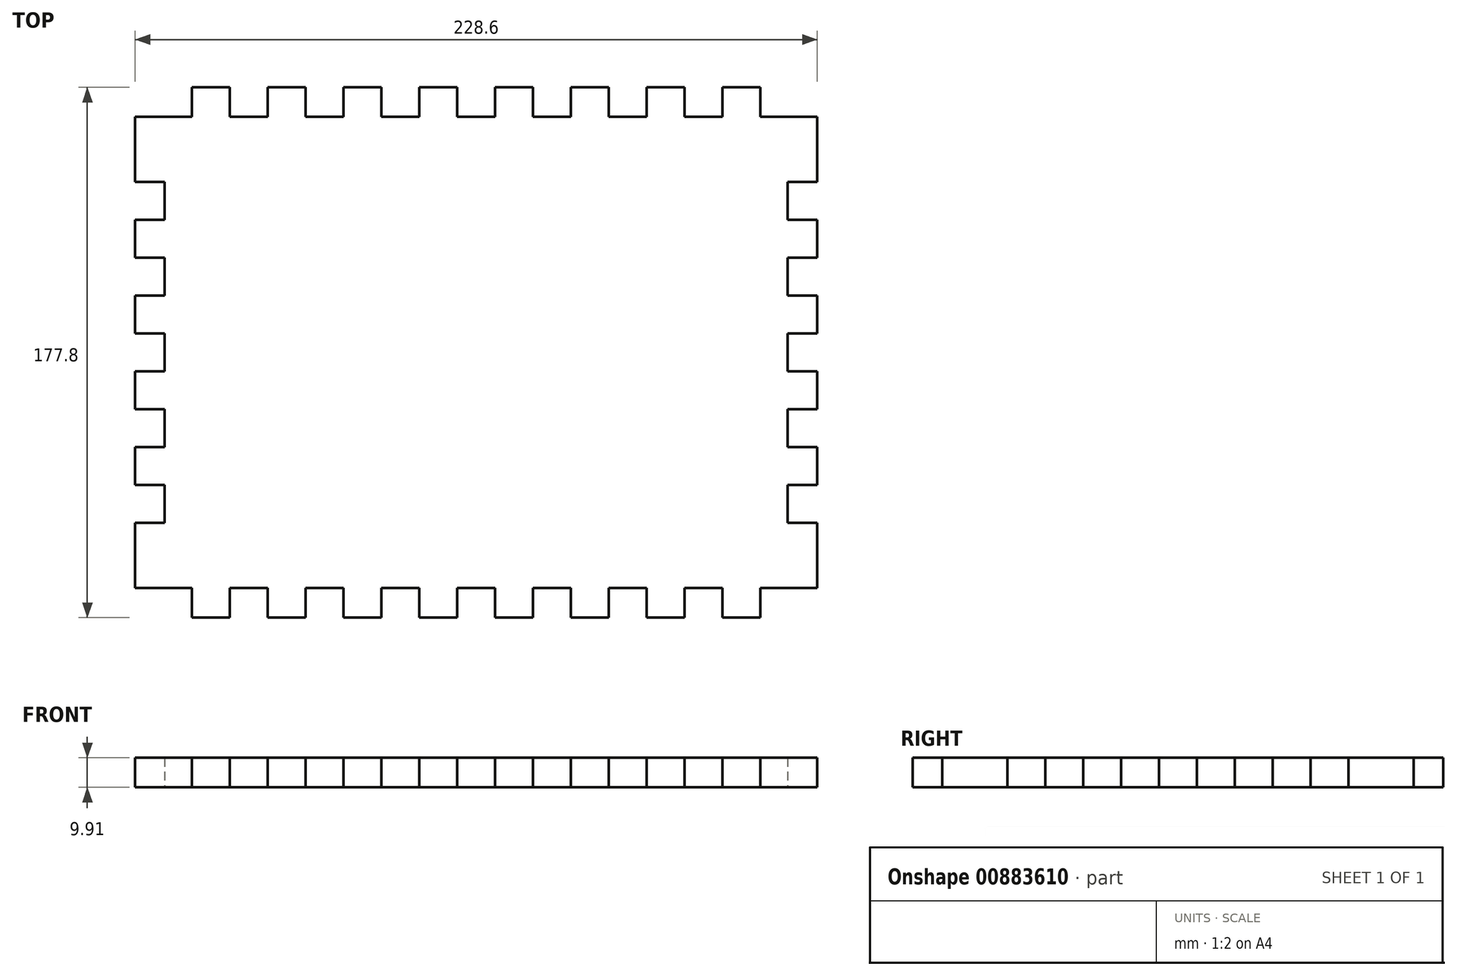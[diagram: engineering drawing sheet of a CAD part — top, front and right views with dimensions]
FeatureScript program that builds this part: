
annotation { "Feature Type Name" : "Feature", "Feature Type Description" : "" }
export const myFeature = defineFeature(function(context is Context, id is Id, definition is map)
    precondition{}
    {
        {
            var Q0;
            Q0=qCreatedBy(makeId("Top.planeOp"),FACE);
            var sketch = newSketch(context, id + "F0", { "sketchPlane" : qUnion([Q0])});
            skLineSegment(sketch, "E0", {"start": v(19.05, -9.9) * mm, "end": v(19.05, 0) * mm});
            skLineSegment(sketch, "E1", {"start": v(19.05, 0) * mm, "end": v(31.75, 0) * mm});
            skLineSegment(sketch, "E2", {"start": v(31.75, 0) * mm, "end": v(31.75, -9.9) * mm});
            skLineSegment(sketch, "E3", {"start": v(31.75, -9.9) * mm, "end": v(44.45, -9.9) * mm});
            skLineSegment(sketch, "E4", {"start": v(44.45, -9.9) * mm, "end": v(44.45, 0) * mm});
            skLineSegment(sketch, "E5", {"start": v(44.45, 0) * mm, "end": v(57.15, 0) * mm});
            skLineSegment(sketch, "E6", {"start": v(57.15, 0) * mm, "end": v(57.15, -9.9) * mm});
            skLineSegment(sketch, "E7", {"start": v(57.15, -9.9) * mm, "end": v(69.85, -9.9) * mm});
            skLineSegment(sketch, "E8", {"start": v(69.85, -9.9) * mm, "end": v(69.85, 0) * mm});
            skLineSegment(sketch, "E9", {"start": v(69.85, 0) * mm, "end": v(82.55, 0) * mm});
            skLineSegment(sketch, "E10", {"start": v(82.55, 0) * mm, "end": v(82.55, -9.9) * mm});
            skLineSegment(sketch, "E11", {"start": v(82.55, -9.9) * mm, "end": v(95.25, -9.9) * mm});
            skLineSegment(sketch, "E12", {"start": v(95.25, -9.9) * mm, "end": v(95.25, 0) * mm});
            skLineSegment(sketch, "E13", {"start": v(95.25, 0) * mm, "end": v(107.95, 0) * mm});
            skLineSegment(sketch, "E14", {"start": v(107.95, 0) * mm, "end": v(107.95, -9.9) * mm});
            skLineSegment(sketch, "E15", {"start": v(107.95, -9.9) * mm, "end": v(120.65, -9.9) * mm});
            skLineSegment(sketch, "E16", {"start": v(120.65, -9.9) * mm, "end": v(120.65, 0) * mm});
            skLineSegment(sketch, "E17", {"start": v(120.65, 0) * mm, "end": v(133.35, 0) * mm});
            skLineSegment(sketch, "E18", {"start": v(133.35, 0) * mm, "end": v(133.35, -9.9) * mm});
            skLineSegment(sketch, "E19", {"start": v(133.35, -9.9) * mm, "end": v(146.05, -9.9) * mm});
            skLineSegment(sketch, "E20", {"start": v(146.05, -9.9) * mm, "end": v(146.05, 0) * mm});
            skLineSegment(sketch, "E21", {"start": v(146.05, 0) * mm, "end": v(158.75, 0) * mm});
            skLineSegment(sketch, "E22", {"start": v(158.75, 0) * mm, "end": v(158.75, -9.9) * mm});
            skLineSegment(sketch, "E23", {"start": v(158.75, -9.9) * mm, "end": v(171.45, -9.9) * mm});
            skLineSegment(sketch, "E24", {"start": v(171.45, -9.9) * mm, "end": v(171.45, 0) * mm});
            skLineSegment(sketch, "E25", {"start": v(171.45, 0) * mm, "end": v(184.15, 0) * mm});
            skLineSegment(sketch, "E26", {"start": v(184.15, 0) * mm, "end": v(184.15, -9.9) * mm});
            skLineSegment(sketch, "E27", {"start": v(184.15, -9.9) * mm, "end": v(196.85, -9.9) * mm});
            skLineSegment(sketch, "E28", {"start": v(196.85, -9.9) * mm, "end": v(196.85, 0) * mm});
            skLineSegment(sketch, "E29", {"start": v(196.85, 0) * mm, "end": v(209.55, 0) * mm});
            skLineSegment(sketch, "E30", {"start": v(209.55, 0) * mm, "end": v(209.55, -9.9) * mm});
            skPoint(sketch, "E31.orphan", {"position": v(0, 0) * mm});
            skPoint(sketch, "E32.orphan", {"position": v(0, -9.9) * mm});
            skLineSegment(sketch, "E33", {"start": v(0, -31.75) * mm, "end": v(9.9, -31.75) * mm});
            skLineSegment(sketch, "E34", {"start": v(9.9, -31.75) * mm, "end": v(9.9, -44.45) * mm});
            skLineSegment(sketch, "E35", {"start": v(9.9, -44.45) * mm, "end": v(0, -44.45) * mm});
            skLineSegment(sketch, "E36", {"start": v(0, -44.45) * mm, "end": v(0, -57.15) * mm});
            skLineSegment(sketch, "E37", {"start": v(0, -57.15) * mm, "end": v(9.9, -57.15) * mm});
            skLineSegment(sketch, "E38", {"start": v(9.9, -57.15) * mm, "end": v(9.9, -69.85) * mm});
            skLineSegment(sketch, "E39", {"start": v(9.9, -69.85) * mm, "end": v(0, -69.85) * mm});
            skLineSegment(sketch, "E40", {"start": v(0, -69.85) * mm, "end": v(0, -82.55) * mm});
            skLineSegment(sketch, "E41", {"start": v(0, -82.55) * mm, "end": v(9.9, -82.55) * mm});
            skLineSegment(sketch, "E42", {"start": v(9.9, -82.55) * mm, "end": v(9.9, -95.25) * mm});
            skLineSegment(sketch, "E43", {"start": v(9.9, -95.25) * mm, "end": v(0, -95.25) * mm});
            skLineSegment(sketch, "E44.trimOffspring", {"start": v(0, -95.25) * mm, "end": v(0, -107.95) * mm});
            skLineSegment(sketch, "E45", {"start": v(0, -107.95) * mm, "end": v(9.9, -107.95) * mm});
            skLineSegment(sketch, "E46", {"start": v(9.9, -107.95) * mm, "end": v(9.9, -120.65) * mm});
            skLineSegment(sketch, "E47", {"start": v(9.9, -120.65) * mm, "end": v(0, -120.65) * mm});
            skLineSegment(sketch, "E48", {"start": v(0, -120.65) * mm, "end": v(0, -133.35) * mm});
            skLineSegment(sketch, "E49", {"start": v(0, -133.35) * mm, "end": v(9.9, -133.35) * mm});
            skLineSegment(sketch, "E50", {"start": v(9.9, -133.35) * mm, "end": v(9.9, -146.05) * mm});
            skLineSegment(sketch, "E51", {"start": v(9.9, -146.05) * mm, "end": v(0, -146.05) * mm});
            skLineSegment(sketch, "E52", {"start": v(114.3, -9.9) * mm, "end": v(114.3, -13.72) * mm, "construction": true});
            skLineSegment(sketch, "E53.MirrorCS", {"start": v(228.6, -95.25) * mm, "end": v(228.6, -107.95) * mm});
            skLineSegment(sketch, "E54.MirrorCS", {"start": v(228.6, -44.45) * mm, "end": v(228.6, -57.15) * mm});
            skLineSegment(sketch, "E55.MirrorCS", {"start": v(228.6, -120.65) * mm, "end": v(228.6, -133.35) * mm});
            skLineSegment(sketch, "E56.MirrorCS", {"start": v(228.6, -69.85) * mm, "end": v(228.6, -82.55) * mm});
            skLineSegment(sketch, "E57.MirrorCS", {"start": v(228.6, -107.95) * mm, "end": v(218.7, -107.95) * mm});
            skLineSegment(sketch, "E58.MirrorCS", {"start": v(228.6, -82.55) * mm, "end": v(218.7, -82.55) * mm});
            skLineSegment(sketch, "E59.MirrorCS", {"start": v(228.6, -133.35) * mm, "end": v(218.7, -133.35) * mm});
            skLineSegment(sketch, "E60.MirrorCS", {"start": v(218.7, -69.85) * mm, "end": v(228.6, -69.85) * mm});
            skLineSegment(sketch, "E61.MirrorCS", {"start": v(218.7, -107.95) * mm, "end": v(218.7, -120.65) * mm});
            skLineSegment(sketch, "E62.MirrorCS", {"start": v(228.6, -57.15) * mm, "end": v(218.7, -57.15) * mm});
            skLineSegment(sketch, "E63.MirrorCS", {"start": v(218.7, -120.65) * mm, "end": v(228.6, -120.65) * mm});
            skLineSegment(sketch, "E64.MirrorCS", {"start": v(218.7, -95.25) * mm, "end": v(228.6, -95.25) * mm});
            skLineSegment(sketch, "E65.MirrorCS", {"start": v(218.7, -57.15) * mm, "end": v(218.7, -69.85) * mm});
            skLineSegment(sketch, "E66.MirrorCS", {"start": v(218.7, -44.45) * mm, "end": v(228.6, -44.45) * mm});
            skLineSegment(sketch, "E67.MirrorCS", {"start": v(218.7, -133.35) * mm, "end": v(218.7, -146.05) * mm});
            skLineSegment(sketch, "E68.MirrorCS", {"start": v(218.7, -146.05) * mm, "end": v(228.6, -146.05) * mm});
            skLineSegment(sketch, "E69.MirrorCS", {"start": v(228.6, -31.75) * mm, "end": v(218.7, -31.75) * mm});
            skLineSegment(sketch, "E70.MirrorCS", {"start": v(218.7, -82.55) * mm, "end": v(218.7, -95.25) * mm});
            skLineSegment(sketch, "E71.MirrorCS", {"start": v(218.7, -31.75) * mm, "end": v(218.7, -44.45) * mm});
            skLineSegment(sketch, "E72", {"start": v(9.9, -88.9) * mm, "end": v(13.72, -88.9) * mm, "construction": true});
            skLineSegment(sketch, "E73.MirrorCS", {"start": v(209.55, -177.8) * mm, "end": v(209.55, -167.9) * mm});
            skLineSegment(sketch, "E74.MirrorCS", {"start": v(158.75, -177.8) * mm, "end": v(158.75, -167.9) * mm});
            skLineSegment(sketch, "E75.MirrorCS", {"start": v(146.05, -167.9) * mm, "end": v(146.05, -177.8) * mm});
            skLineSegment(sketch, "E76.MirrorCS", {"start": v(19.05, -167.9) * mm, "end": v(19.05, -177.8) * mm});
            skLineSegment(sketch, "E77.MirrorCS", {"start": v(69.85, -167.9) * mm, "end": v(69.85, -177.8) * mm});
            skLineSegment(sketch, "E78.MirrorCS", {"start": v(196.85, -167.9) * mm, "end": v(196.85, -177.8) * mm});
            skLineSegment(sketch, "E79.MirrorCS", {"start": v(82.55, -177.8) * mm, "end": v(82.55, -167.9) * mm});
            skLineSegment(sketch, "E80.MirrorCS", {"start": v(171.45, -167.9) * mm, "end": v(171.45, -177.8) * mm});
            skLineSegment(sketch, "E81.MirrorCS", {"start": v(146.05, -177.8) * mm, "end": v(158.75, -177.8) * mm});
            skLineSegment(sketch, "E82.MirrorCS", {"start": v(107.95, -177.8) * mm, "end": v(107.95, -167.9) * mm});
            skLineSegment(sketch, "E83.MirrorCS", {"start": v(120.65, -167.9) * mm, "end": v(120.65, -177.8) * mm});
            skLineSegment(sketch, "E84.MirrorCS", {"start": v(95.25, -167.9) * mm, "end": v(95.25, -177.8) * mm});
            skLineSegment(sketch, "E85.MirrorCS", {"start": v(44.45, -167.9) * mm, "end": v(44.45, -177.8) * mm});
            skLineSegment(sketch, "E86.MirrorCS", {"start": v(31.75, -177.8) * mm, "end": v(31.75, -167.9) * mm});
            skLineSegment(sketch, "E87.MirrorCS", {"start": v(184.15, -177.8) * mm, "end": v(184.15, -167.9) * mm});
            skLineSegment(sketch, "E88.MirrorCS", {"start": v(133.35, -177.8) * mm, "end": v(133.35, -167.9) * mm});
            skLineSegment(sketch, "E89.MirrorCS", {"start": v(57.15, -177.8) * mm, "end": v(57.15, -167.9) * mm});
            skLineSegment(sketch, "E90.MirrorCS", {"start": v(107.95, -167.9) * mm, "end": v(120.65, -167.9) * mm});
            skLineSegment(sketch, "E91.MirrorCS", {"start": v(19.05, -177.8) * mm, "end": v(31.75, -177.8) * mm});
            skLineSegment(sketch, "E92.MirrorCS", {"start": v(31.75, -167.9) * mm, "end": v(44.45, -167.9) * mm});
            skLineSegment(sketch, "E93.MirrorCS", {"start": v(95.25, -177.8) * mm, "end": v(107.95, -177.8) * mm});
            skLineSegment(sketch, "E94.MirrorCS", {"start": v(196.85, -177.8) * mm, "end": v(209.55, -177.8) * mm});
            skLineSegment(sketch, "E95.MirrorCS", {"start": v(158.75, -167.9) * mm, "end": v(171.45, -167.9) * mm});
            skLineSegment(sketch, "E96.MirrorCS", {"start": v(133.35, -167.9) * mm, "end": v(146.05, -167.9) * mm});
            skLineSegment(sketch, "E97.MirrorCS", {"start": v(171.45, -177.8) * mm, "end": v(184.15, -177.8) * mm});
            skLineSegment(sketch, "E98.MirrorCS", {"start": v(69.85, -177.8) * mm, "end": v(82.55, -177.8) * mm});
            skLineSegment(sketch, "E99.MirrorCS", {"start": v(44.45, -177.8) * mm, "end": v(57.15, -177.8) * mm});
            skLineSegment(sketch, "E100.MirrorCS", {"start": v(184.15, -167.9) * mm, "end": v(196.85, -167.9) * mm});
            skLineSegment(sketch, "E101.MirrorCS", {"start": v(82.55, -167.9) * mm, "end": v(95.25, -167.9) * mm});
            skLineSegment(sketch, "E102.MirrorCS", {"start": v(120.65, -177.8) * mm, "end": v(133.35, -177.8) * mm});
            skLineSegment(sketch, "E103.MirrorCS", {"start": v(57.15, -167.9) * mm, "end": v(69.85, -167.9) * mm});
            skLineSegment(sketch, "E104", {"start": v(0, -9.9) * mm, "end": v(0, -31.75) * mm});
            skLineSegment(sketch, "E105", {"start": v(0, -9.9) * mm, "end": v(19.05, -9.9) * mm});
            skLineSegment(sketch, "E106.MirrorCS", {"start": v(0, -167.9) * mm, "end": v(19.05, -167.9) * mm});
            skLineSegment(sketch, "E107.MirrorCS", {"start": v(0, -167.9) * mm, "end": v(0, -146.05) * mm});
            skPoint(sketch, "E108.MirrorCS.end.orphan", {"position": v(209.55, -9.9) * mm});
            skLineSegment(sketch, "E109.MirrorCS", {"start": v(228.6, -9.9) * mm, "end": v(209.55, -9.9) * mm});
            skLineSegment(sketch, "E110.MirrorCS", {"start": v(228.6, -9.9) * mm, "end": v(228.6, -31.75) * mm});
            skLineSegment(sketch, "E111.MirrorCS", {"start": v(228.6, -167.9) * mm, "end": v(209.55, -167.9) * mm});
            skLineSegment(sketch, "E112.MirrorCS", {"start": v(228.6, -167.9) * mm, "end": v(228.6, -146.05) * mm});
            skSolve(sketch);
        }
        {
            var Q0;
            Q0=makeQuery(id+"F0.imprint","IMPRINT",FACE,{"disambiguationData":[TD([[makeQuery(id+"F0.imprint","IMPRINT",EDGE,{"derivedFrom":sQuery(id+"F0.wireOp",EDGE,"E0")}),-1.0]])]});
            extrude(context, id + "F1", {"entities" : qUnion([Q0]), "depth" : 9.9 * mm, "offsetDistance" : 25.4 * mm});
        }
    });
